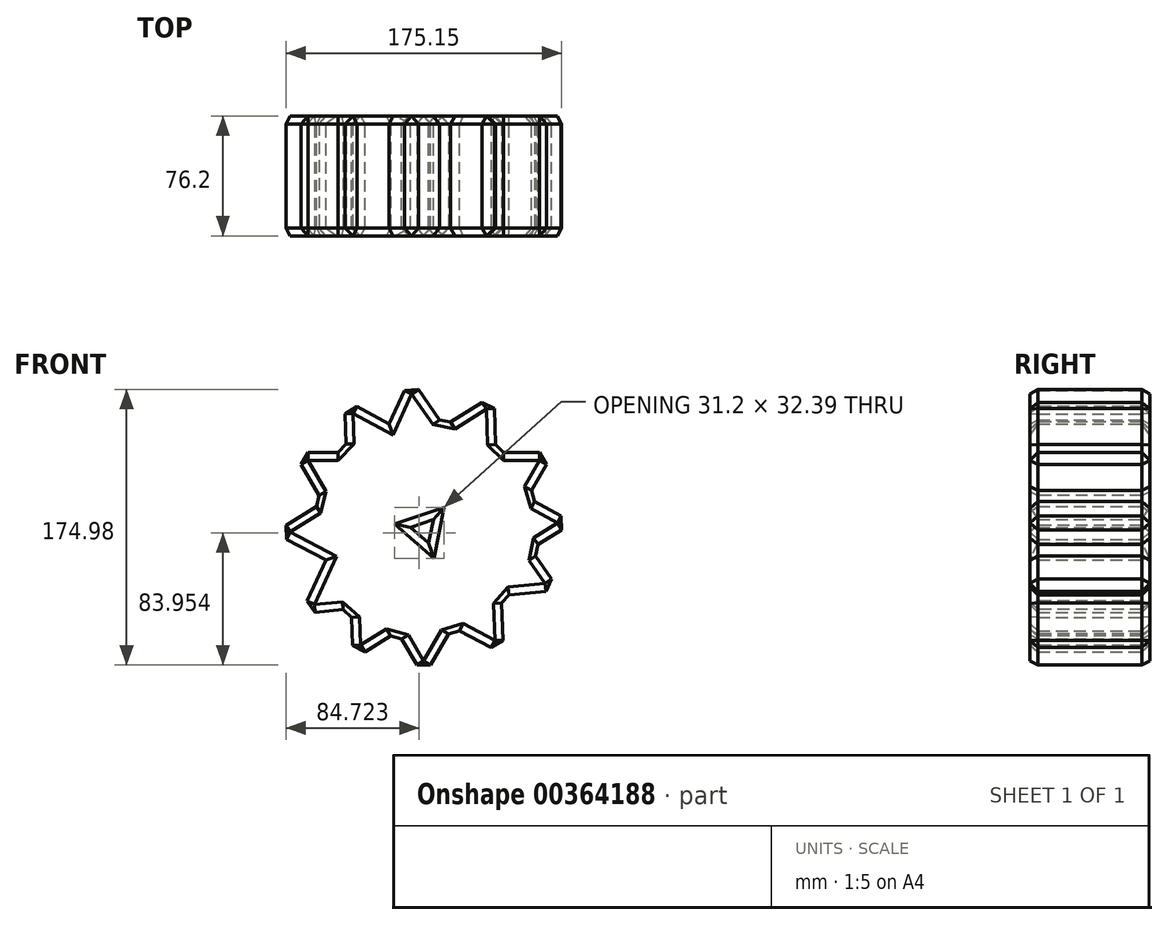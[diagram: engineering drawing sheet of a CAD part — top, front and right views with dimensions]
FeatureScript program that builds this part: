
annotation { "Feature Type Name" : "Feature", "Feature Type Description" : "" }
export const myFeature = defineFeature(function(context is Context, id is Id, definition is map)
    precondition{}
    {
        {
            var Q0;
            Q0=qCreatedBy(makeId("Front.planeOp"),FACE);
            var sketch = newSketch(context, id + "F0", { "sketchPlane" : qUnion([Q0])});
            skCircle(sketch, "E0.cCircle", {"center": v(0, 0) * mm, "radius": 95.1 * mm, "construction": true});
            skLineSegment(sketch, "E0.0", {"start": v(-77.74, -54.77) * mm, "end": v(-8.57, 94.7) * mm});
            skLineSegment(sketch, "E0.1", {"start": v(-8.57, 94.7) * mm, "end": v(86.3, -39.94) * mm});
            skLineSegment(sketch, "E0.2", {"start": v(86.3, -39.94) * mm, "end": v(-77.74, -54.77) * mm});
            skLineSegment(sketch, "E1.0", {"start": v(0, -95.1) * mm, "end": v(-82.35, 47.55) * mm});
            skLineSegment(sketch, "E1.1", {"start": v(-82.35, 47.55) * mm, "end": v(82.35, 47.55) * mm});
            skLineSegment(sketch, "E1.2", {"start": v(82.35, 47.55) * mm, "end": v(0, -95.1) * mm});
            skLineSegment(sketch, "E2.0", {"start": v(-44.9, -83.83) * mm, "end": v(-50.15, 80.8) * mm});
            skLineSegment(sketch, "E2.1", {"start": v(-50.15, 80.8) * mm, "end": v(95.05, 3.04) * mm});
            skLineSegment(sketch, "E2.2", {"start": v(95.05, 3.04) * mm, "end": v(-44.9, -83.83) * mm});
            skLineSegment(sketch, "E3.0", {"start": v(50.55, -80.54) * mm, "end": v(-95.03, -3.5) * mm});
            skLineSegment(sketch, "E3.1", {"start": v(-95.03, -3.5) * mm, "end": v(44.48, 84.05) * mm});
            skLineSegment(sketch, "E3.2", {"start": v(44.48, 84.05) * mm, "end": v(50.55, -80.54) * mm});
            skCircle(sketch, "E4.cCircle", {"center": v(0.24, -1.7) * mm, "radius": 8.9 * mm, "construction": true});
            skLineSegment(sketch, "E4.0", {"start": v(-8.48, 0) * mm, "end": v(6.08, 5.01) * mm});
            skLineSegment(sketch, "E4.1", {"start": v(6.08, 5.01) * mm, "end": v(3.14, -10.1) * mm});
            skLineSegment(sketch, "E4.2", {"start": v(3.14, -10.1) * mm, "end": v(-8.48, 0) * mm});
            skSolve(sketch);
        }
        {
            var Q0;
            {var subQ0=sQuery(id+"F0.wireOp",EDGE,"E2.1");var subQ1=sQuery(id+"F0.wireOp",EDGE,"E0.0");var subQ2=makeQuery(id+"F0.imprint","INTERSECT",VERTEX,{"derivedFrom":[subQ1,subQ0]});Q0=makeQuery(id+"F0.imprint","IMPRINT",FACE,{"disambiguationData":[TD([[makeQuery(id+"F0.imprint","IMPRINT",EDGE,{"disambiguationData":[TD([[subQ2,1.0]])],"derivedFrom":subQ1}),-1.0]])]});}
            var Q1;
            {var subQ0=sQuery(id+"F0.wireOp",EDGE,"E1.2");var subQ1=sQuery(id+"F0.wireOp",EDGE,"E1.0");var subQ2=makeQuery(id+"F0.imprint","INTERSECT",VERTEX,{"derivedFrom":[subQ1,subQ0]});Q1=makeQuery(id+"F0.imprint","IMPRINT",FACE,{"disambiguationData":[TD([[makeQuery(id+"F0.imprint","IMPRINT",EDGE,{"disambiguationData":[TD([[subQ2,-1.0]])],"derivedFrom":subQ1}),-1.0]])]});}
            var Q2;
            {var subQ0=sQuery(id+"F0.wireOp",EDGE,"E3.1");var subQ1=sQuery(id+"F0.wireOp",EDGE,"E0.1");var subQ2=makeQuery(id+"F0.imprint","INTERSECT",VERTEX,{"derivedFrom":[subQ1,subQ0]});Q2=makeQuery(id+"F0.imprint","IMPRINT",FACE,{"disambiguationData":[TD([[makeQuery(id+"F0.imprint","IMPRINT",EDGE,{"disambiguationData":[TD([[subQ2,-1.0]])],"derivedFrom":subQ1}),-1.0]])]});}
            var Q3;
            {var subQ0=sQuery(id+"F0.wireOp",EDGE,"E3.2");var subQ1=sQuery(id+"F0.wireOp",EDGE,"E0.1");var subQ2=makeQuery(id+"F0.imprint","INTERSECT",VERTEX,{"derivedFrom":[subQ1,subQ0]});Q3=makeQuery(id+"F0.imprint","IMPRINT",FACE,{"disambiguationData":[TD([[makeQuery(id+"F0.imprint","IMPRINT",EDGE,{"disambiguationData":[TD([[subQ2,-1.0]])],"derivedFrom":subQ1}),1.0]])]});}
            var Q4;
            {var subQ0=sQuery(id+"F0.wireOp",EDGE,"E3.0");var subQ1=sQuery(id+"F0.wireOp",EDGE,"E0.0");var subQ2=makeQuery(id+"F0.imprint","INTERSECT",VERTEX,{"derivedFrom":[subQ1,subQ0]});Q4=makeQuery(id+"F0.imprint","IMPRINT",FACE,{"disambiguationData":[TD([[makeQuery(id+"F0.imprint","IMPRINT",EDGE,{"disambiguationData":[TD([[subQ2,-1.0]])],"derivedFrom":subQ1}),-1.0]])]});}
            var Q5;
            {var subQ0=sQuery(id+"F0.wireOp",EDGE,"E3.0");var subQ1=sQuery(id+"F0.wireOp",EDGE,"E0.2");var subQ2=makeQuery(id+"F0.imprint","INTERSECT",VERTEX,{"derivedFrom":[subQ1,subQ0]});Q5=makeQuery(id+"F0.imprint","IMPRINT",FACE,{"disambiguationData":[TD([[makeQuery(id+"F0.imprint","IMPRINT",EDGE,{"disambiguationData":[TD([[subQ2,-1.0]])],"derivedFrom":subQ1}),1.0]])]});}
            var Q6;
            {var subQ0=sQuery(id+"F0.wireOp",EDGE,"E2.1");var subQ1=sQuery(id+"F0.wireOp",EDGE,"E0.1");var subQ2=makeQuery(id+"F0.imprint","INTERSECT",VERTEX,{"derivedFrom":[subQ1,subQ0]});Q6=makeQuery(id+"F0.imprint","IMPRINT",FACE,{"disambiguationData":[TD([[makeQuery(id+"F0.imprint","IMPRINT",EDGE,{"disambiguationData":[TD([[subQ2,-1.0]])],"derivedFrom":subQ1}),1.0]])]});}
            var Q7;
            {var subQ0=sQuery(id+"F0.wireOp",EDGE,"E3.1");var subQ1=sQuery(id+"F0.wireOp",EDGE,"E0.1");var subQ2=makeQuery(id+"F0.imprint","INTERSECT",VERTEX,{"derivedFrom":[subQ1,subQ0]});Q7=makeQuery(id+"F0.imprint","IMPRINT",FACE,{"disambiguationData":[TD([[makeQuery(id+"F0.imprint","IMPRINT",EDGE,{"disambiguationData":[TD([[subQ2,-1.0]])],"derivedFrom":subQ1}),1.0]])]});}
            var Q8;
            {var subQ0=sQuery(id+"F0.wireOp",EDGE,"E0.1");var subQ1=sQuery(id+"F0.wireOp",EDGE,"E0.0");var subQ2=makeQuery(id+"F0.imprint","INTERSECT",VERTEX,{"derivedFrom":[subQ1,subQ0]});Q8=makeQuery(id+"F0.imprint","IMPRINT",FACE,{"disambiguationData":[TD([[makeQuery(id+"F0.imprint","IMPRINT",EDGE,{"disambiguationData":[TD([[subQ2,1.0]])],"derivedFrom":subQ1}),-1.0]])]});}
            var Q9;
            {var subQ0=sQuery(id+"F0.wireOp",EDGE,"E0.2");var subQ1=sQuery(id+"F0.wireOp",EDGE,"E0.0");var subQ2=makeQuery(id+"F0.imprint","INTERSECT",VERTEX,{"derivedFrom":[subQ1,subQ0]});Q9=makeQuery(id+"F0.imprint","IMPRINT",FACE,{"disambiguationData":[TD([[makeQuery(id+"F0.imprint","IMPRINT",EDGE,{"disambiguationData":[TD([[subQ2,-1.0]])],"derivedFrom":subQ1}),-1.0]])]});}
            var Q10;
            {var subQ0=sQuery(id+"F0.wireOp",EDGE,"E1.2");var subQ1=sQuery(id+"F0.wireOp",EDGE,"E0.2");var subQ2=makeQuery(id+"F0.imprint","INTERSECT",VERTEX,{"derivedFrom":[subQ1,subQ0]});Q10=makeQuery(id+"F0.imprint","IMPRINT",FACE,{"disambiguationData":[TD([[makeQuery(id+"F0.imprint","IMPRINT",EDGE,{"disambiguationData":[TD([[subQ2,-1.0]])],"derivedFrom":subQ1}),-1.0]])]});}
            var Q11;
            {var subQ0=sQuery(id+"F0.wireOp",EDGE,"E1.1");var subQ1=sQuery(id+"F0.wireOp",EDGE,"E0.1");var subQ2=makeQuery(id+"F0.imprint","INTERSECT",VERTEX,{"derivedFrom":[subQ1,subQ0]});Q11=makeQuery(id+"F0.imprint","IMPRINT",FACE,{"disambiguationData":[TD([[makeQuery(id+"F0.imprint","IMPRINT",EDGE,{"disambiguationData":[TD([[subQ2,-1.0]])],"derivedFrom":subQ1}),1.0]])]});}
            var Q12;
            Q12=makeQuery(id+"F0.imprint","IMPRINT",FACE,{"disambiguationData":[TD([[makeQuery(id+"F0.imprint","IMPRINT",EDGE,{"derivedFrom":sQuery(id+"F0.wireOp",EDGE,"E4.0")}),1.0]])]});
            var Q13;
            {var subQ0=sQuery(id+"F0.wireOp",EDGE,"E1.1");var subQ1=sQuery(id+"F0.wireOp",EDGE,"E1.0");var subQ2=makeQuery(id+"F0.imprint","INTERSECT",VERTEX,{"derivedFrom":[subQ1,subQ0]});Q13=makeQuery(id+"F0.imprint","IMPRINT",FACE,{"disambiguationData":[TD([[makeQuery(id+"F0.imprint","IMPRINT",EDGE,{"disambiguationData":[TD([[subQ2,1.0]])],"derivedFrom":subQ1}),-1.0]])]});}
            var Q14;
            {var subQ0=sQuery(id+"F0.wireOp",EDGE,"E3.2");var subQ1=sQuery(id+"F0.wireOp",EDGE,"E0.2");var subQ2=makeQuery(id+"F0.imprint","INTERSECT",VERTEX,{"derivedFrom":[subQ1,subQ0]});Q14=makeQuery(id+"F0.imprint","IMPRINT",FACE,{"disambiguationData":[TD([[makeQuery(id+"F0.imprint","IMPRINT",EDGE,{"disambiguationData":[TD([[subQ2,-1.0]])],"derivedFrom":subQ1}),1.0]])]});}
            var Q15;
            {var subQ0=sQuery(id+"F0.wireOp",EDGE,"E3.0");var subQ1=sQuery(id+"F0.wireOp",EDGE,"E0.2");var subQ2=makeQuery(id+"F0.imprint","INTERSECT",VERTEX,{"derivedFrom":[subQ1,subQ0]});Q15=makeQuery(id+"F0.imprint","IMPRINT",FACE,{"disambiguationData":[TD([[makeQuery(id+"F0.imprint","IMPRINT",EDGE,{"disambiguationData":[TD([[subQ2,-1.0]])],"derivedFrom":subQ1}),-1.0]])]});}
            var Q16;
            {var subQ0=sQuery(id+"F0.wireOp",EDGE,"E3.2");var subQ1=sQuery(id+"F0.wireOp",EDGE,"E1.2");var subQ2=makeQuery(id+"F0.imprint","INTERSECT",VERTEX,{"derivedFrom":[subQ1,subQ0]});Q16=makeQuery(id+"F0.imprint","IMPRINT",FACE,{"disambiguationData":[TD([[makeQuery(id+"F0.imprint","IMPRINT",EDGE,{"disambiguationData":[TD([[subQ2,-1.0]])],"derivedFrom":subQ1}),1.0]])]});}
            var Q17;
            {var subQ0=sQuery(id+"F0.wireOp",EDGE,"E3.2");var subQ1=sQuery(id+"F0.wireOp",EDGE,"E0.1");var subQ2=makeQuery(id+"F0.imprint","INTERSECT",VERTEX,{"derivedFrom":[subQ1,subQ0]});Q17=makeQuery(id+"F0.imprint","IMPRINT",FACE,{"disambiguationData":[TD([[makeQuery(id+"F0.imprint","IMPRINT",EDGE,{"disambiguationData":[TD([[subQ2,-1.0]])],"derivedFrom":subQ1}),-1.0]])]});}
            var Q18;
            {var subQ0=sQuery(id+"F0.wireOp",EDGE,"E3.0");var subQ1=sQuery(id+"F0.wireOp",EDGE,"E0.0");var subQ2=makeQuery(id+"F0.imprint","INTERSECT",VERTEX,{"derivedFrom":[subQ1,subQ0]});Q18=makeQuery(id+"F0.imprint","IMPRINT",FACE,{"disambiguationData":[TD([[makeQuery(id+"F0.imprint","IMPRINT",EDGE,{"disambiguationData":[TD([[subQ2,-1.0]])],"derivedFrom":subQ1}),1.0]])]});}
            var Q19;
            {var subQ0=sQuery(id+"F0.wireOp",EDGE,"E2.1");var subQ1=sQuery(id+"F0.wireOp",EDGE,"E0.0");var subQ2=makeQuery(id+"F0.imprint","INTERSECT",VERTEX,{"derivedFrom":[subQ1,subQ0]});Q19=makeQuery(id+"F0.imprint","IMPRINT",FACE,{"disambiguationData":[TD([[makeQuery(id+"F0.imprint","IMPRINT",EDGE,{"disambiguationData":[TD([[subQ2,1.0]])],"derivedFrom":subQ1}),1.0]])]});}
            var Q20;
            {var subQ0=sQuery(id+"F0.wireOp",EDGE,"E3.1");var subQ1=sQuery(id+"F0.wireOp",EDGE,"E0.0");var subQ2=makeQuery(id+"F0.imprint","INTERSECT",VERTEX,{"derivedFrom":[subQ1,subQ0]});Q20=makeQuery(id+"F0.imprint","IMPRINT",FACE,{"disambiguationData":[TD([[makeQuery(id+"F0.imprint","IMPRINT",EDGE,{"disambiguationData":[TD([[subQ2,-1.0]])],"derivedFrom":subQ1}),-1.0]])]});}
            var Q21;
            {var subQ0=sQuery(id+"F0.wireOp",EDGE,"E2.0");var subQ1=sQuery(id+"F0.wireOp",EDGE,"E0.2");var subQ2=makeQuery(id+"F0.imprint","INTERSECT",VERTEX,{"derivedFrom":[subQ1,subQ0]});Q21=makeQuery(id+"F0.imprint","IMPRINT",FACE,{"disambiguationData":[TD([[makeQuery(id+"F0.imprint","IMPRINT",EDGE,{"disambiguationData":[TD([[subQ2,1.0]])],"derivedFrom":subQ1}),-1.0]])]});}
            var Q22;
            {var subQ0=sQuery(id+"F0.wireOp",EDGE,"E1.1");var subQ1=sQuery(id+"F0.wireOp",EDGE,"E0.1");var subQ2=makeQuery(id+"F0.imprint","INTERSECT",VERTEX,{"derivedFrom":[subQ1,subQ0]});Q22=makeQuery(id+"F0.imprint","IMPRINT",FACE,{"disambiguationData":[TD([[makeQuery(id+"F0.imprint","IMPRINT",EDGE,{"disambiguationData":[TD([[subQ2,-1.0]])],"derivedFrom":subQ1}),-1.0]])]});}
            var Q23;
            {var subQ0=sQuery(id+"F0.wireOp",EDGE,"E2.2");var subQ1=sQuery(id+"F0.wireOp",EDGE,"E0.2");var subQ2=makeQuery(id+"F0.imprint","INTERSECT",VERTEX,{"derivedFrom":[subQ1,subQ0]});Q23=makeQuery(id+"F0.imprint","IMPRINT",FACE,{"disambiguationData":[TD([[makeQuery(id+"F0.imprint","IMPRINT",EDGE,{"disambiguationData":[TD([[subQ2,-1.0]])],"derivedFrom":subQ1}),1.0]])]});}
            var Q24;
            {var subQ0=sQuery(id+"F0.wireOp",EDGE,"E3.1");var subQ1=sQuery(id+"F0.wireOp",EDGE,"E1.1");var subQ2=makeQuery(id+"F0.imprint","INTERSECT",VERTEX,{"derivedFrom":[subQ1,subQ0]});Q24=makeQuery(id+"F0.imprint","IMPRINT",FACE,{"disambiguationData":[TD([[makeQuery(id+"F0.imprint","IMPRINT",EDGE,{"disambiguationData":[TD([[subQ2,-1.0]])],"derivedFrom":subQ1}),1.0]])]});}
            var Q25;
            {var subQ0=sQuery(id+"F0.wireOp",EDGE,"E3.1");var subQ1=sQuery(id+"F0.wireOp",EDGE,"E0.0");var subQ2=makeQuery(id+"F0.imprint","INTERSECT",VERTEX,{"derivedFrom":[subQ1,subQ0]});Q25=makeQuery(id+"F0.imprint","IMPRINT",FACE,{"disambiguationData":[TD([[makeQuery(id+"F0.imprint","IMPRINT",EDGE,{"disambiguationData":[TD([[subQ2,-1.0]])],"derivedFrom":subQ1}),1.0]])]});}
            var Q26;
            {var subQ0=sQuery(id+"F0.wireOp",EDGE,"E1.2");var subQ1=sQuery(id+"F0.wireOp",EDGE,"E0.2");var subQ2=makeQuery(id+"F0.imprint","INTERSECT",VERTEX,{"derivedFrom":[subQ1,subQ0]});Q26=makeQuery(id+"F0.imprint","IMPRINT",FACE,{"disambiguationData":[TD([[makeQuery(id+"F0.imprint","IMPRINT",EDGE,{"disambiguationData":[TD([[subQ2,-1.0]])],"derivedFrom":subQ1}),1.0]])]});}
            var Q27;
            {var subQ0=sQuery(id+"F0.wireOp",EDGE,"E1.0");var subQ1=sQuery(id+"F0.wireOp",EDGE,"E0.0");var subQ2=makeQuery(id+"F0.imprint","INTERSECT",VERTEX,{"derivedFrom":[subQ1,subQ0]});Q27=makeQuery(id+"F0.imprint","IMPRINT",FACE,{"disambiguationData":[TD([[makeQuery(id+"F0.imprint","IMPRINT",EDGE,{"disambiguationData":[TD([[subQ2,-1.0]])],"derivedFrom":subQ1}),1.0]])]});}
            var Q28;
            {var subQ0=sQuery(id+"F0.wireOp",EDGE,"E2.0");var subQ1=sQuery(id+"F0.wireOp",EDGE,"E0.2");var subQ2=makeQuery(id+"F0.imprint","INTERSECT",VERTEX,{"derivedFrom":[subQ1,subQ0]});Q28=makeQuery(id+"F0.imprint","IMPRINT",FACE,{"disambiguationData":[TD([[makeQuery(id+"F0.imprint","IMPRINT",EDGE,{"disambiguationData":[TD([[subQ2,1.0]])],"derivedFrom":subQ1}),1.0]])]});}
            var Q29;
            {var subQ0=sQuery(id+"F0.wireOp",EDGE,"E1.2");var subQ1=sQuery(id+"F0.wireOp",EDGE,"E1.1");var subQ2=makeQuery(id+"F0.imprint","INTERSECT",VERTEX,{"derivedFrom":[subQ1,subQ0]});Q29=makeQuery(id+"F0.imprint","IMPRINT",FACE,{"disambiguationData":[TD([[makeQuery(id+"F0.imprint","IMPRINT",EDGE,{"disambiguationData":[TD([[subQ2,1.0]])],"derivedFrom":subQ1}),-1.0]])]});}
            var Q30;
            {var subQ0=sQuery(id+"F0.wireOp",EDGE,"E0.2");var subQ1=sQuery(id+"F0.wireOp",EDGE,"E0.1");var subQ2=makeQuery(id+"F0.imprint","INTERSECT",VERTEX,{"derivedFrom":[subQ1,subQ0]});Q30=makeQuery(id+"F0.imprint","IMPRINT",FACE,{"disambiguationData":[TD([[makeQuery(id+"F0.imprint","IMPRINT",EDGE,{"disambiguationData":[TD([[subQ2,1.0]])],"derivedFrom":subQ1}),-1.0]])]});}
            var Q31;
            {var subQ0=sQuery(id+"F0.wireOp",EDGE,"E2.2");var subQ1=sQuery(id+"F0.wireOp",EDGE,"E0.1");var subQ2=makeQuery(id+"F0.imprint","INTERSECT",VERTEX,{"derivedFrom":[subQ1,subQ0]});Q31=makeQuery(id+"F0.imprint","IMPRINT",FACE,{"disambiguationData":[TD([[makeQuery(id+"F0.imprint","IMPRINT",EDGE,{"disambiguationData":[TD([[subQ2,1.0]])],"derivedFrom":subQ1}),-1.0]])]});}
            var Q32;
            {var subQ0=sQuery(id+"F0.wireOp",EDGE,"E3.0");var subQ1=sQuery(id+"F0.wireOp",EDGE,"E1.0");var subQ2=makeQuery(id+"F0.imprint","INTERSECT",VERTEX,{"derivedFrom":[subQ1,subQ0]});Q32=makeQuery(id+"F0.imprint","IMPRINT",FACE,{"disambiguationData":[TD([[makeQuery(id+"F0.imprint","IMPRINT",EDGE,{"disambiguationData":[TD([[subQ2,-1.0]])],"derivedFrom":subQ1}),1.0]])]});}
            var Q33;
            {var subQ0=sQuery(id+"F0.wireOp",EDGE,"E2.0");var subQ1=sQuery(id+"F0.wireOp",EDGE,"E0.0");var subQ2=makeQuery(id+"F0.imprint","INTERSECT",VERTEX,{"derivedFrom":[subQ1,subQ0]});Q33=makeQuery(id+"F0.imprint","IMPRINT",FACE,{"disambiguationData":[TD([[makeQuery(id+"F0.imprint","IMPRINT",EDGE,{"disambiguationData":[TD([[subQ2,-1.0]])],"derivedFrom":subQ1}),1.0]])]});}
            var Q34;
            {var subQ0=sQuery(id+"F0.wireOp",EDGE,"E3.2");var subQ1=sQuery(id+"F0.wireOp",EDGE,"E0.2");var subQ2=makeQuery(id+"F0.imprint","INTERSECT",VERTEX,{"derivedFrom":[subQ1,subQ0]});Q34=makeQuery(id+"F0.imprint","IMPRINT",FACE,{"disambiguationData":[TD([[makeQuery(id+"F0.imprint","IMPRINT",EDGE,{"disambiguationData":[TD([[subQ2,-1.0]])],"derivedFrom":subQ1}),-1.0]])]});}
            var Q35;
            {var subQ0=sQuery(id+"F0.wireOp",EDGE,"E2.2");var subQ1=sQuery(id+"F0.wireOp",EDGE,"E0.1");var subQ2=makeQuery(id+"F0.imprint","INTERSECT",VERTEX,{"derivedFrom":[subQ1,subQ0]});Q35=makeQuery(id+"F0.imprint","IMPRINT",FACE,{"disambiguationData":[TD([[makeQuery(id+"F0.imprint","IMPRINT",EDGE,{"disambiguationData":[TD([[subQ2,1.0]])],"derivedFrom":subQ1}),1.0]])]});}
            var Q36;
            {var subQ0=sQuery(id+"F0.wireOp",EDGE,"E1.0");var subQ1=sQuery(id+"F0.wireOp",EDGE,"E0.0");var subQ2=makeQuery(id+"F0.imprint","INTERSECT",VERTEX,{"derivedFrom":[subQ1,subQ0]});Q36=makeQuery(id+"F0.imprint","IMPRINT",FACE,{"disambiguationData":[TD([[makeQuery(id+"F0.imprint","IMPRINT",EDGE,{"disambiguationData":[TD([[subQ2,-1.0]])],"derivedFrom":subQ1}),-1.0]])]});}
            extrude(context, id + "F1", {"entities" : qUnion([Q0, Q1, Q2, Q3, Q4, Q5, Q6, Q7, Q8, Q9, Q10, Q11, Q12, Q13, Q14, Q15, Q16, Q17, Q18, Q19, Q20, Q21, Q22, Q23, Q24, Q25, Q26, Q27, Q28, Q29, Q30, Q31, Q32, Q33, Q34, Q35, Q36]), "depth" : 76.2 * mm});
        }
        {
            var Q0;
            Q0=makeQuery(id+"F1.opExtrude","CAP_FACE",FACE,{"disambiguationData":[OSD([sQuery(id+"F0.wireOp",EDGE,"E0.0"),sQuery(id+"F0.wireOp",EDGE,"E0.1"),sQuery(id+"F0.wireOp",EDGE,"E0.2"),sQuery(id+"F0.wireOp",EDGE,"E1.0"),sQuery(id+"F0.wireOp",EDGE,"E1.1"),sQuery(id+"F0.wireOp",EDGE,"E1.2"),sQuery(id+"F0.wireOp",EDGE,"E2.0"),sQuery(id+"F0.wireOp",EDGE,"E2.1"),sQuery(id+"F0.wireOp",EDGE,"E2.2"),sQuery(id+"F0.wireOp",EDGE,"E3.0"),sQuery(id+"F0.wireOp",EDGE,"E3.1"),sQuery(id+"F0.wireOp",EDGE,"E3.2"),sQuery(id+"F0.wireOp",EDGE,"E4.0"),sQuery(id+"F0.wireOp",EDGE,"E4.1"),sQuery(id+"F0.wireOp",EDGE,"E4.2")])],"isStart":false});
            var Q1;
            Q1=makeQuery(id+"F1.opExtrude","CAP_FACE",FACE,{"disambiguationData":[OSD([sQuery(id+"F0.wireOp",EDGE,"E0.0"),sQuery(id+"F0.wireOp",EDGE,"E0.1"),sQuery(id+"F0.wireOp",EDGE,"E0.2"),sQuery(id+"F0.wireOp",EDGE,"E1.0"),sQuery(id+"F0.wireOp",EDGE,"E1.1"),sQuery(id+"F0.wireOp",EDGE,"E1.2"),sQuery(id+"F0.wireOp",EDGE,"E2.0"),sQuery(id+"F0.wireOp",EDGE,"E2.1"),sQuery(id+"F0.wireOp",EDGE,"E2.2"),sQuery(id+"F0.wireOp",EDGE,"E3.0"),sQuery(id+"F0.wireOp",EDGE,"E3.1"),sQuery(id+"F0.wireOp",EDGE,"E3.2"),sQuery(id+"F0.wireOp",EDGE,"E4.0"),sQuery(id+"F0.wireOp",EDGE,"E4.1"),sQuery(id+"F0.wireOp",EDGE,"E4.2")])],"isStart":true});
            var Q2;
            {var subQ0=sQuery(id+"F0.wireOp",EDGE,"E1.0");Q2=makeQuery(id+"F1.opExtrude","SWEPT_FACE",FACE,{"disambiguationData":[OSD([subQ0]),TDD([makeQuery(id+"F0.imprint","IMPRINT",EDGE,{"disambiguationData":[TD([[makeQuery(id+"F0.imprint","INTERSECT",VERTEX,{"derivedFrom":[subQ0,sQuery(id+"F0.wireOp",EDGE,"E1.1")]}),1.0]])],"derivedFrom":subQ0})])]});}
            var Q3;
            {var subQ0=sQuery(id+"F0.wireOp",EDGE,"E2.0");Q3=makeQuery(id+"F1.opExtrude","SWEPT_FACE",FACE,{"disambiguationData":[OSD([subQ0]),TDD([makeQuery(id+"F0.imprint","IMPRINT",EDGE,{"disambiguationData":[TD([[makeQuery(id+"F0.imprint","INTERSECT",VERTEX,{"derivedFrom":[subQ0,sQuery(id+"F0.wireOp",EDGE,"E2.1")]}),1.0]])],"derivedFrom":subQ0})])]});}
            var Q4;
            {var subQ0=sQuery(id+"F0.wireOp",EDGE,"E1.1");Q4=makeQuery(id+"F1.opExtrude","SWEPT_FACE",FACE,{"disambiguationData":[OSD([subQ0]),TDD([makeQuery(id+"F0.imprint","IMPRINT",EDGE,{"disambiguationData":[TD([[makeQuery(id+"F0.imprint","INTERSECT",VERTEX,{"derivedFrom":[sQuery(id+"F0.wireOp",EDGE,"E1.0"),subQ0]}),-1.0]])],"derivedFrom":subQ0})])]});}
            var Q5;
            {var subQ0=sQuery(id+"F0.wireOp",EDGE,"E3.1");Q5=makeQuery(id+"F1.opExtrude","SWEPT_FACE",FACE,{"disambiguationData":[OSD([subQ0]),TDD([makeQuery(id+"F0.imprint","IMPRINT",EDGE,{"disambiguationData":[TD([[makeQuery(id+"F0.imprint","INTERSECT",VERTEX,{"derivedFrom":[sQuery(id+"F0.wireOp",EDGE,"E3.0"),subQ0]}),-1.0]])],"derivedFrom":subQ0})])]});}
            var Q6;
            {var subQ0=sQuery(id+"F0.wireOp",EDGE,"E0.1");Q6=makeQuery(id+"F1.opExtrude","SWEPT_FACE",FACE,{"disambiguationData":[OSD([subQ0]),TDD([makeQuery(id+"F0.imprint","IMPRINT",EDGE,{"disambiguationData":[TD([[makeQuery(id+"F0.imprint","INTERSECT",VERTEX,{"derivedFrom":[sQuery(id+"F0.wireOp",EDGE,"E0.0"),subQ0]}),-1.0]])],"derivedFrom":subQ0})])]});}
            var Q7;
            {var subQ0=sQuery(id+"F0.wireOp",EDGE,"E3.2");Q7=makeQuery(id+"F1.opExtrude","SWEPT_FACE",FACE,{"disambiguationData":[OSD([subQ0]),TDD([makeQuery(id+"F0.imprint","IMPRINT",EDGE,{"disambiguationData":[TD([[makeQuery(id+"F0.imprint","INTERSECT",VERTEX,{"derivedFrom":[sQuery(id+"F0.wireOp",EDGE,"E3.1"),subQ0]}),-1.0]])],"derivedFrom":subQ0})])]});}
            var Q8;
            {var subQ0=sQuery(id+"F0.wireOp",EDGE,"E2.1");Q8=makeQuery(id+"F1.opExtrude","SWEPT_FACE",FACE,{"disambiguationData":[OSD([subQ0]),TDD([makeQuery(id+"F0.imprint","IMPRINT",EDGE,{"disambiguationData":[TD([[makeQuery(id+"F0.imprint","INTERSECT",VERTEX,{"derivedFrom":[subQ0,sQuery(id+"F0.wireOp",EDGE,"E2.2")]}),1.0]])],"derivedFrom":subQ0})])]});}
            var Q9;
            {var subQ0=sQuery(id+"F0.wireOp",EDGE,"E1.2");Q9=makeQuery(id+"F1.opExtrude","SWEPT_FACE",FACE,{"disambiguationData":[OSD([subQ0]),TDD([makeQuery(id+"F0.imprint","IMPRINT",EDGE,{"disambiguationData":[TD([[makeQuery(id+"F0.imprint","INTERSECT",VERTEX,{"derivedFrom":[sQuery(id+"F0.wireOp",EDGE,"E1.1"),subQ0]}),-1.0]])],"derivedFrom":subQ0})])]});}
            var Q10;
            {var subQ0=sQuery(id+"F0.wireOp",EDGE,"E0.1");Q10=makeQuery(id+"F1.opExtrude","SWEPT_FACE",FACE,{"disambiguationData":[OSD([subQ0]),TDD([makeQuery(id+"F0.imprint","IMPRINT",EDGE,{"disambiguationData":[TD([[makeQuery(id+"F0.imprint","INTERSECT",VERTEX,{"derivedFrom":[subQ0,sQuery(id+"F0.wireOp",EDGE,"E0.2")]}),1.0]])],"derivedFrom":subQ0})])]});}
            var Q11;
            {var subQ0=sQuery(id+"F0.wireOp",EDGE,"E0.2");Q11=makeQuery(id+"F1.opExtrude","SWEPT_FACE",FACE,{"disambiguationData":[OSD([subQ0]),TDD([makeQuery(id+"F0.imprint","IMPRINT",EDGE,{"disambiguationData":[TD([[makeQuery(id+"F0.imprint","INTERSECT",VERTEX,{"derivedFrom":[sQuery(id+"F0.wireOp",EDGE,"E0.0"),subQ0]}),1.0]])],"derivedFrom":subQ0})])]});}
            var Q12;
            {var subQ0=sQuery(id+"F0.wireOp",EDGE,"E2.2");Q12=makeQuery(id+"F1.opExtrude","SWEPT_FACE",FACE,{"disambiguationData":[OSD([subQ0]),TDD([makeQuery(id+"F0.imprint","IMPRINT",EDGE,{"disambiguationData":[TD([[makeQuery(id+"F0.imprint","INTERSECT",VERTEX,{"derivedFrom":[sQuery(id+"F0.wireOp",EDGE,"E2.0"),subQ0]}),1.0]])],"derivedFrom":subQ0})])]});}
            var Q13;
            {var subQ0=sQuery(id+"F0.wireOp",EDGE,"E1.2");Q13=makeQuery(id+"F1.opExtrude","SWEPT_FACE",FACE,{"disambiguationData":[OSD([subQ0]),TDD([makeQuery(id+"F0.imprint","IMPRINT",EDGE,{"disambiguationData":[TD([[makeQuery(id+"F0.imprint","INTERSECT",VERTEX,{"derivedFrom":[sQuery(id+"F0.wireOp",EDGE,"E1.0"),subQ0]}),1.0]])],"derivedFrom":subQ0})])]});}
            var Q14;
            {var subQ0=sQuery(id+"F0.wireOp",EDGE,"E3.2");Q14=makeQuery(id+"F1.opExtrude","SWEPT_FACE",FACE,{"disambiguationData":[OSD([subQ0]),TDD([makeQuery(id+"F0.imprint","IMPRINT",EDGE,{"disambiguationData":[TD([[makeQuery(id+"F0.imprint","INTERSECT",VERTEX,{"derivedFrom":[sQuery(id+"F0.wireOp",EDGE,"E3.0"),subQ0]}),1.0]])],"derivedFrom":subQ0})])]});}
            chamfer(context, id + "F2", {"entities" : qUnion([Q0, Q1, Q2, Q3, Q4, Q5, Q6, Q7, Q8, Q9, Q10, Q11, Q12, Q13, Q14]), "width" : 5.08 * mm, "tangentPropagation" : true});
        }
    });
